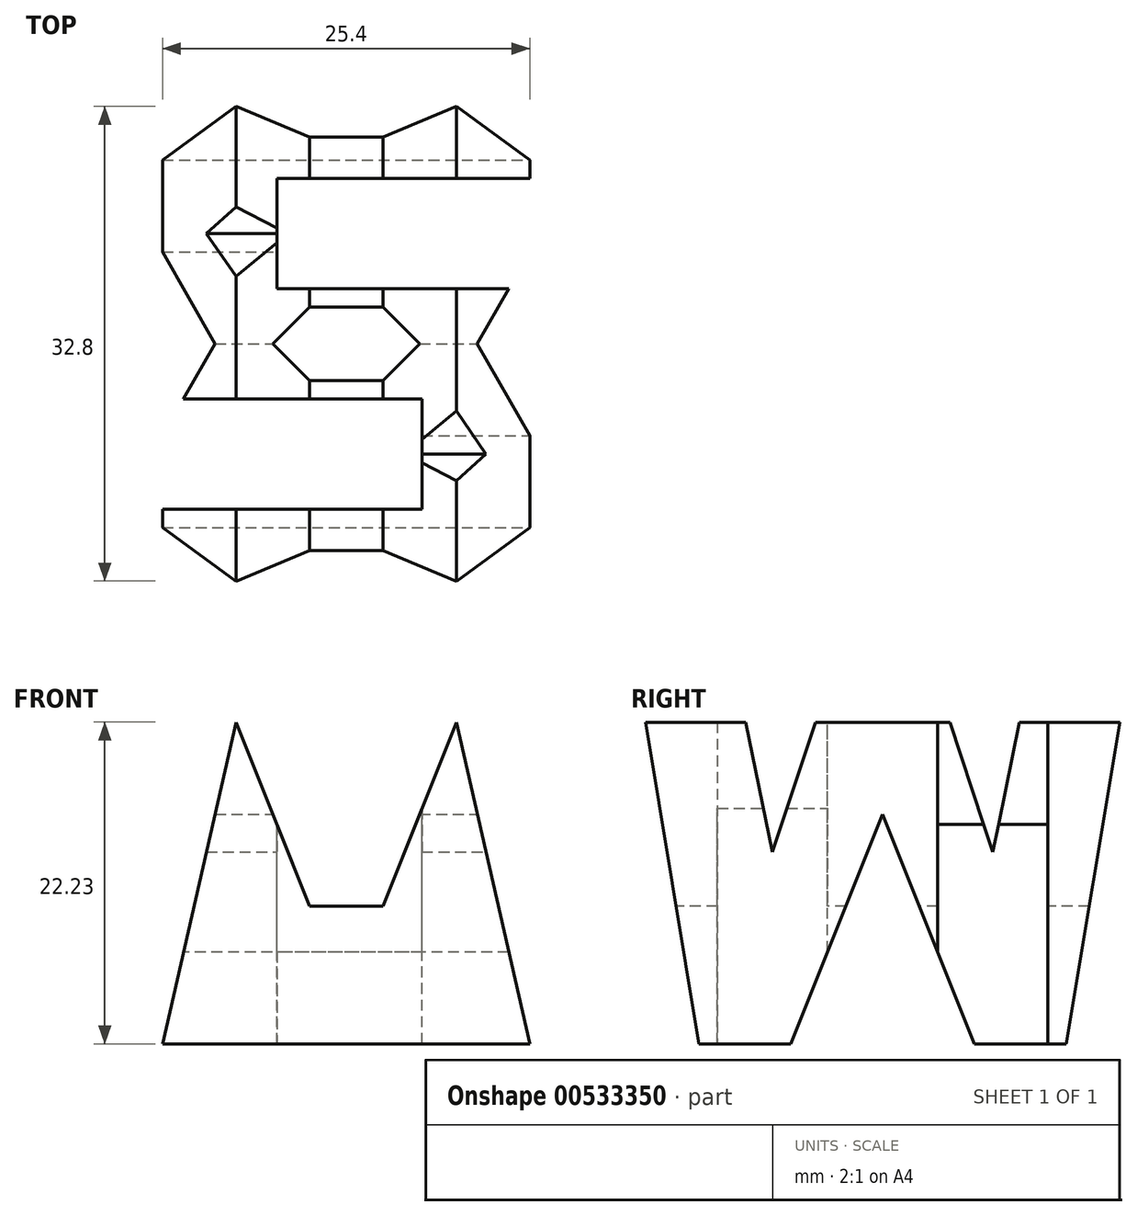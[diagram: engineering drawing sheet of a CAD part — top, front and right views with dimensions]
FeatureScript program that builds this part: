
annotation { "Feature Type Name" : "Feature", "Feature Type Description" : "" }
export const myFeature = defineFeature(function(context is Context, id is Id, definition is map)
    precondition{}
    {
        {
            var Q0;
            Q0=qCreatedBy(makeId("Front.planeOp"),FACE);
            var sketch = newSketch(context, id + "F0", { "sketchPlane" : qUnion([Q0])});
            skLineSegment(sketch, "E0", {"start": v(0, 0) * mm, "end": v(0, 38.1) * mm});
            skLineSegment(sketch, "E1", {"start": v(38.1, 38.1) * mm, "end": v(38.1, 0) * mm});
            skLineSegment(sketch, "E2", {"start": v(0, 0) * mm, "end": v(38.1, 0) * mm});
            skLineSegment(sketch, "E3", {"start": v(0, 38.1) * mm, "end": v(38.1, 38.1) * mm});
            skSolve(sketch);
        }
        {
            var Q0;
            Q0=makeQuery(id+"F0.imprint","IMPRINT",FACE,{"disambiguationData":[TD([[makeQuery(id+"F0.imprint","IMPRINT",EDGE,{"derivedFrom":sQuery(id+"F0.wireOp",EDGE,"E0")}),-1.0]])]});
            extrude(context, id + "F1", {"entities" : qUnion([Q0]), "depth" : 38.1 * mm, "offsetDistance" : 25.4 * mm});
        }
        {
            var Q0;
            Q0=qCreatedBy(makeId("Front.planeOp"),FACE);
            cPlane(context, id + "F2", {"entities" : qUnion([Q0]), "cplaneType" : CPlaneType.OFFSET, "offset" : 38.1 * mm, "width" : 152.4 * mm, "height" : 152.4 * mm});
        }
        {
            var Q0;
            Q0=qCreatedBy(makeId("Right.planeOp"),FACE);
            cPlane(context, id + "F3", {"entities" : qUnion([Q0]), "cplaneType" : CPlaneType.OFFSET, "offset" : 38.1 * mm, "width" : 152.4 * mm, "height" : 152.4 * mm});
        }
        {
            var Q0;
            Q0=qCreatedBy(makeId("Top.planeOp"),FACE);
            cPlane(context, id + "F4", {"entities" : qUnion([Q0]), "cplaneType" : CPlaneType.OFFSET, "offset" : 38.1 * mm, "width" : 152.4 * mm, "height" : 152.4 * mm});
        }
        {
            var Q0;
            Q0=qCreatedBy(id+"F3.planeOp",FACE);
            var sketch = newSketch(context, id + "F5", { "sketchPlane" : qUnion([Q0])});
            skLineSegment(sketch, "E4", {"start": v(0, 0) * mm, "end": v(0, 38.1) * mm});
            skLineSegment(sketch, "E5", {"start": v(0, 38.1) * mm, "end": v(-38.1, 38.1) * mm});
            skLineSegment(sketch, "E6", {"start": v(-38.1, 38.1) * mm, "end": v(-38.1, 0) * mm});
            skLineSegment(sketch, "E7", {"start": v(-31.75, 0) * mm, "end": v(-25.4, 0) * mm});
            skLineSegment(sketch, "E8", {"start": v(-12.7, 0) * mm, "end": v(-6.35, 0) * mm});
            skLineSegment(sketch, "E9", {"start": v(-38.1, 38.1) * mm, "end": v(-31.75, 38.1) * mm});
            skPoint(sketch, "E10.end.orphan", {"position": v(-16.7, 17.3) * mm});
            skPoint(sketch, "E11.start.orphan", {"position": v(-0.55, 17.3) * mm});
            skLineSegment(sketch, "E12.trimOffspring", {"start": v(-12.7, 0) * mm, "end": v(0, 0) * mm});
            skLineSegment(sketch, "E13", {"start": v(0, 38.1) * mm, "end": v(-9.26, 38.1) * mm});
            skPoint(sketch, "E14.start.orphan", {"position": v(-9.74, 14.94) * mm});
            skPoint(sketch, "E15.start.orphan", {"position": v(-19.05, 17.3) * mm});
            skPoint(sketch, "E16.end.orphan", {"position": v(-26.67, 14.94) * mm});
            skLineSegment(sketch, "E17", {"start": v(-38.1, 38.1) * mm, "end": v(-31.75, 0) * mm});
            skLineSegment(sketch, "E18", {"start": v(-25.4, 0) * mm, "end": v(-19.05, 15.87) * mm});
            skLineSegment(sketch, "E19", {"start": v(-19.05, 15.88) * mm, "end": v(-12.7, 0) * mm});
            skLineSegment(sketch, "E20", {"start": v(-6.35, 0) * mm, "end": v(0, 38.1) * mm});
            skLineSegment(sketch, "E21", {"start": v(0, 38.1) * mm, "end": v(-6.35, 38.1) * mm});
            skLineSegment(sketch, "E22", {"start": v(-6.35, 38.1) * mm, "end": v(-11.43, 13.26) * mm});
            skLineSegment(sketch, "E23", {"start": v(-11.43, 13.26) * mm, "end": v(-16.5, 28.57) * mm});
            skLineSegment(sketch, "E24", {"start": v(-16.5, 28.57) * mm, "end": v(-21.59, 28.57) * mm});
            skLineSegment(sketch, "E25", {"start": v(-21.59, 28.57) * mm, "end": v(-26.67, 13.26) * mm});
            skLineSegment(sketch, "E26", {"start": v(-26.67, 13.26) * mm, "end": v(-31.75, 38.1) * mm});
            skLineSegment(sketch, "E27", {"start": v(-38.1, 0) * mm, "end": v(0, 0) * mm});
            skSolve(sketch);
        }
        {
            var Q0;
            Q0=makeQuery(id+"F5.imprint","IMPRINT",FACE,{"disambiguationData":[TD([[makeQuery(id+"F5.imprint","IMPRINT",EDGE,{"derivedFrom":sQuery(id+"F5.wireOp",EDGE,"E5")}),1.0]])]});
            var Q1;
            {var subQ0=sQuery(id+"F5.wireOp",EDGE,"E6");Q1=makeQuery(id+"F5.imprint","IMPRINT",FACE,{"disambiguationData":[TD([[makeQuery(id+"F5.imprint","IMPRINT",EDGE,{"derivedFrom":subQ0}),1.0]])]});}
            var Q2;
            {var subQ0=sQuery(id+"F5.wireOp",EDGE,"E18");Q2=makeQuery(id+"F5.imprint","IMPRINT",FACE,{"disambiguationData":[TD([[makeQuery(id+"F5.imprint","IMPRINT",EDGE,{"derivedFrom":subQ0}),-1.0]])]});}
            var Q3;
            {var subQ0=sQuery(id+"F5.wireOp",EDGE,"E4");Q3=makeQuery(id+"F5.imprint","IMPRINT",FACE,{"disambiguationData":[TD([[makeQuery(id+"F5.imprint","IMPRINT",EDGE,{"derivedFrom":subQ0}),1.0]])]});}
            extrude(context, id + "F6", {"entities" : qUnion([Q0, Q1, Q2, Q3]), "operationType" : NewBodyOperationType.REMOVE, "oppositeDirection" : true, "depth" : 38.1 * mm, "offsetDistance" : 25.4 * mm});
        }
        {
            var Q0;
            Q0=qCreatedBy(id+"F2.planeOp",FACE);
            var sketch = newSketch(context, id + "F7", { "sketchPlane" : qUnion([Q0])});
            skLineSegment(sketch, "E28", {"start": v(38.1, 38.1) * mm, "end": v(38.1, 0) * mm});
            skLineSegment(sketch, "E29", {"start": v(38.1, 38.1) * mm, "end": v(0, 38.1) * mm});
            skLineSegment(sketch, "E30", {"start": v(0, 38.1) * mm, "end": v(0, 0) * mm});
            skLineSegment(sketch, "E31", {"start": v(0, 0) * mm, "end": v(38.1, 0) * mm});
            skLineSegment(sketch, "E32", {"start": v(0, 0) * mm, "end": v(6.35, 38.1) * mm});
            skLineSegment(sketch, "E33", {"start": v(6.35, 38.1) * mm, "end": v(12.7, 38.1) * mm});
            skLineSegment(sketch, "E34", {"start": v(12.7, 38.1) * mm, "end": v(19.05, 17.01) * mm});
            skLineSegment(sketch, "E35", {"start": v(19.05, 17.01) * mm, "end": v(25.4, 38.1) * mm});
            skLineSegment(sketch, "E36", {"start": v(25.4, 38.1) * mm, "end": v(31.75, 38.1) * mm});
            skLineSegment(sketch, "E37", {"start": v(31.75, 38.1) * mm, "end": v(38.1, 0) * mm});
            skLineSegment(sketch, "E38", {"start": v(38.1, 0) * mm, "end": v(31.75, 0) * mm});
            skLineSegment(sketch, "E39", {"start": v(31.75, 0) * mm, "end": v(26.67, 22.22) * mm});
            skLineSegment(sketch, "E40", {"start": v(11.43, 22.23) * mm, "end": v(6.35, 0) * mm});
            skLineSegment(sketch, "E41", {"start": v(6.35, 0) * mm, "end": v(0, 0) * mm});
            skPoint(sketch, "E42.end.orphan", {"position": v(19.05, 9.88) * mm});
            skLineSegment(sketch, "E43", {"start": v(11.43, 22.22) * mm, "end": v(16.51, 9.52) * mm});
            skLineSegment(sketch, "E44", {"start": v(16.51, 9.52) * mm, "end": v(21.6, 9.52) * mm});
            skLineSegment(sketch, "E45", {"start": v(21.6, 9.52) * mm, "end": v(26.67, 22.22) * mm});
            skSolve(sketch);
        }
        {
            var Q0;
            {var subQ0=sQuery(id+"F7.wireOp",EDGE,"E30");Q0=makeQuery(id+"F7.imprint","IMPRINT",FACE,{"disambiguationData":[TD([[makeQuery(id+"F7.imprint","IMPRINT",EDGE,{"derivedFrom":subQ0}),1.0]])]});}
            var Q1;
            {var subQ0=sQuery(id+"F7.wireOp",EDGE,"E34");Q1=makeQuery(id+"F7.imprint","IMPRINT",FACE,{"disambiguationData":[TD([[makeQuery(id+"F7.imprint","IMPRINT",EDGE,{"derivedFrom":subQ0}),1.0]])]});}
            var Q2;
            Q2=makeQuery(id+"F7.imprint","IMPRINT",FACE,{"disambiguationData":[TD([[makeQuery(id+"F7.imprint","IMPRINT",EDGE,{"derivedFrom":sQuery(id+"F7.wireOp",EDGE,"E31")}),1.0]])]});
            var Q3;
            {var subQ0=sQuery(id+"F7.wireOp",EDGE,"E28");Q3=makeQuery(id+"F7.imprint","IMPRINT",FACE,{"disambiguationData":[TD([[makeQuery(id+"F7.imprint","IMPRINT",EDGE,{"derivedFrom":subQ0}),-1.0]])]});}
            extrude(context, id + "F8", {"entities" : qUnion([Q0, Q1, Q2, Q3]), "operationType" : NewBodyOperationType.REMOVE, "oppositeDirection" : true, "depth" : 38.1 * mm, "offsetDistance" : 25.4 * mm});
        }
        {
            var Q0;
            Q0=qCreatedBy(id+"F4.planeOp",FACE);
            var sketch = newSketch(context, id + "F9", { "sketchPlane" : qUnion([Q0])});
            skLineSegment(sketch, "E46", {"start": v(38.1, 0) * mm, "end": v(38.1, -38.1) * mm});
            skLineSegment(sketch, "E47", {"start": v(38.1, -38.1) * mm, "end": v(0, -38.1) * mm});
            skLineSegment(sketch, "E48", {"start": v(0, -38.1) * mm, "end": v(0, -22.86) * mm});
            skPoint(sketch, "E49.startSnap0", {"position": v(37.45, -30.26) * mm});
            skLineSegment(sketch, "E50", {"start": v(0, 0) * mm, "end": v(38.1, 0) * mm});
            skLineSegment(sketch, "E51", {"start": v(14.25, -15.24) * mm, "end": v(38.1, -15.24) * mm});
            skLineSegment(sketch, "E52", {"start": v(38.1, -15.24) * mm, "end": v(38.1, -7.62) * mm});
            skLineSegment(sketch, "E53", {"start": v(0, -22.86) * mm, "end": v(24.29, -22.86) * mm});
            skLineSegment(sketch, "E54", {"start": v(24.29, -22.86) * mm, "end": v(24.29, -30.48) * mm});
            skLineSegment(sketch, "E55", {"start": v(24.29, -30.48) * mm, "end": v(0, -30.48) * mm});
            skLineSegment(sketch, "E56", {"start": v(0, -30.48) * mm, "end": v(0, -22.86) * mm});
            skLineSegment(sketch, "E57", {"start": v(38.1, -7.62) * mm, "end": v(14.25, -7.62) * mm});
            skLineSegment(sketch, "E58", {"start": v(14.25, -7.62) * mm, "end": v(14.25, -15.24) * mm});
            skLineSegment(sketch, "E59", {"start": v(0, 0) * mm, "end": v(0, -38.1) * mm});
            skLineSegment(sketch, "E60", {"start": v(0, -38.1) * mm, "end": v(13.32, -38.1) * mm});
            skLineSegment(sketch, "E61", {"start": v(13.32, -38.1) * mm, "end": v(0, -38.1) * mm});
            skSolve(sketch);
        }
        {
            var Q0;
            Q0=makeQuery(id+"F9.imprint","IMPRINT",FACE,{"disambiguationData":[TD([[makeQuery(id+"F9.imprint","IMPRINT",EDGE,{"derivedFrom":sQuery(id+"F9.wireOp",EDGE,"E51")}),1.0]])]});
            var Q1;
            {var subQ0=sQuery(id+"F9.wireOp",EDGE,"E53");Q1=makeQuery(id+"F9.imprint","IMPRINT",FACE,{"disambiguationData":[TD([[makeQuery(id+"F9.imprint","IMPRINT",EDGE,{"derivedFrom":subQ0}),-1.0]])]});}
            extrude(context, id + "F10", {"entities" : qUnion([Q0, Q1]), "operationType" : NewBodyOperationType.REMOVE, "oppositeDirection" : true, "depth" : 38.1 * mm, "offsetDistance" : 25.4 * mm});
        }
    });
